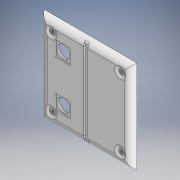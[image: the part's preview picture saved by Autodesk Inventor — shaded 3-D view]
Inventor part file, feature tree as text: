
AUTODESK INVENTOR PART (.ipt)
format: ipt  version: 2018 (Build 220112000, 112)  size: 367,104 bytes
history: native  units: in
note: dims shown in document units (in); Inventor stores cm internally (conversion verified against a paired STEP export)
features: extrude x14, sketch x14, fillet x5, chamfer x1
ambient origin geometry x8: Origin, YZ Plane, XZ Plane, XY Plane, X Axis, Y Axis, Z Axis, Center Point
bodies: Solid1 (feature_tree)
feature tree (34):
  extrude  "Extrusion1"  Depth=4.5in
  extrude  "Extrusion2"  Depth=0.1575in
  extrude  "Extrusion3"  Depth=1.125in
  fillet  "Fillet1"  Radius=1.125in
  sketch  "Sketch4"  dims[d8=0.25in d9=0.0in d10=0.0984in d11=0.0984in]
  sketch  "Sketch5"  dims[d12=0.0787in d13=0.0in d14=0.3937in]
  extrude  "Extrusion6"  Depth=0.0984in
  fillet  "Fillet4"  Radius=0.0984in
  extrude  "Extrusion7"  Depth=0.3937in
  extrude  "Extrusion8"  Depth=4.0in
  extrude  "Extrusion9"  Depth=0.0394in TaperAngle=0.0deg
  fillet  "Fillet6"  Radius=0.4724in
  fillet  "Fillet7"  Radius=0.0625in
  extrude  "Extrusion10"  Depth=0.25in TaperAngle=0.0deg
  extrude  "Extrusion11"  Depth=3.375in
  extrude  "Extrusion12"  Depth=0.1772in
  fillet  "Fillet8"  Radius=0.1772in
  extrude  "Extrusion13"  Depth=0.25in TaperAngle=0.0deg
  extrude  "Extrusion14"  Depth=0.3051in
  chamfer  "Chamfer1"  Distance=0.0591in
  extrude  "Extrusion15"  Depth=0.1969in
  extrude  "Extrusion16"  Depth=0.1969in
  sketch  "Sketch1"  dims[d0=4.5in d1=4.5in]
  sketch  "Sketch2"  dims[d2=0.1575in d3=0.0in d4=0.6299in]
  sketch  "Sketch3"  dims[d5=0.6299in d6=1.125in d7=1.125in]
  sketch  "Sketch6"  dims[d23=4.0in d24=4.0in]
  sketch  "Sketch7"  dims[d29=0.125in d30=0.0394in d31=0.0in d34=0.4724in d35=0.0625in]
  sketch  "Sketch8"  dims[d36=0.0625in d37=0.25in d38=0.0in]
  sketch  "Sketch9"  dims[d43=3.375in d44=3.375in]
  sketch  "Sketch10"  dims[d45=0.1772in d46=0.1772in d47=0.1772in]
  sketch  "Sketch11"  dims[d48=0.1772in d49=0.25in d50=0.0in]
  sketch  "Sketch12"  dims[d52=0.3051in d53=0.3051in]
  sketch  "Sketch13"  dims[d54=0.3051in]
  sketch  "Sketch14"  dims[d55=0.3051in d56=0.0591in d57=0.0in d58=0.1969in d59=0.1969in d60=0.0689in d61=0.9646in d62=0.0689in d63=0.4823in d64=0.4823in d65=1.3583in d66=0.6791in d67=0.6791in d68=0.0689in d69=0.0689in d70=1.4567in d71=0.1969in d72=0.1969in d73=0.1969in d74=0.1969in d75=0.0787in d76=0.0in d77=0.1575in d78=0.3937in d79=0.5906in d80=0.0in d81=0.4626in d82=0.7874in d83=0.0in d84=0.1181in d85=0.1969in d86=0.7283in d87=0.7283in d88=0.7283in d89=0.7283in d90=0.0394in d91=0.0in d92=1.0433in d94=0.1181in d95=0.0in d97=0.0in d98=0.1083in d99=0.0394in d100=0.125in d101=45.0deg d102=0.315in d103=0.0in d104=1.0in d105=0.5906in d106=0.5906in d107=0.0787in d108=0.0in]
